# Revit family: Shower-Handshower-KOHLER-Citrus-K-12861M
name_source: partatom
category: Plumbing Fixtures
revit_build: Autodesk Revit 2015 (Build: 20140606_1530(x64)
units: mm (PartAtom-declared; Revit-internal decimal feet)

## types (1)
- CP-Polished Chrome
    ADA Compliant = No
    Assembly Code = D2010700
    CW Connection = No
    Cold Water Inlet = Cold Water Inlet
    Date Modified = 08/02/2019
    Default Elevation = 0"
    Description = Multifunction handshower
    Drain Included = No
    Finish = Kohler-Metal-CP-Polished_Chrome
    Flow Rate = 3 GPM
    HW Connection = Yes
    Height = 8 7/8"
    Hot Water Inlet = Tempered Water Inlet
    Length = 3 7/16"
    Manufacturer = KOHLER Co.
    MasterFormat 1995 = 15410
    MasterFormat 2004 = 22.41.23
    Material = Premium Metal Construction
    Model = K-12861M-CP
    Pressure = 80.00 psi
    Product Documentation Link = http://resources.kohler.com
    Product Name = Citrus
    Product Page URL = https://la.kohler.com
    URL = https://la.kohler.com
    Vent Connection = No
    Waste Connection = No
    Waste Water Outlet = Waste Water Outlet
    WaterSense Certified = No
    Width = 3 9/16"

## geometry (parser evidence)
native form markers: Sweep x5
no freeform markers — native parametric forms only
